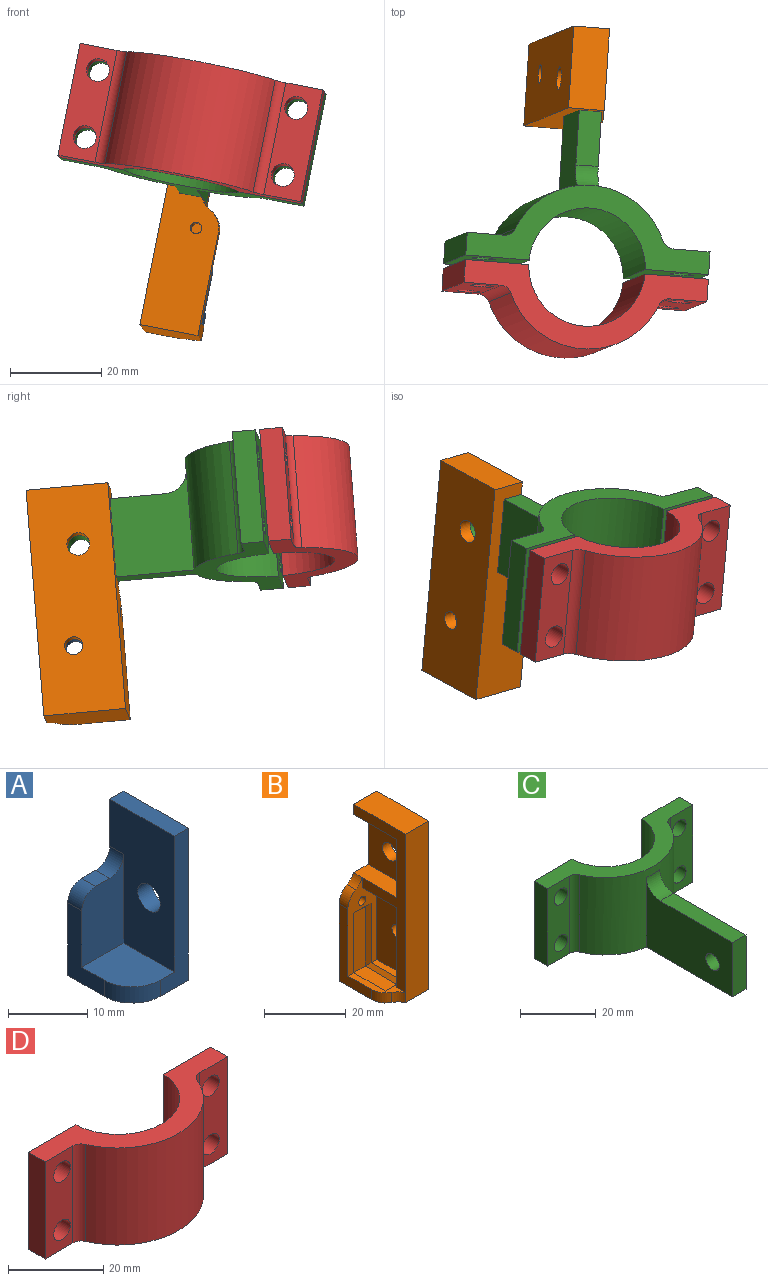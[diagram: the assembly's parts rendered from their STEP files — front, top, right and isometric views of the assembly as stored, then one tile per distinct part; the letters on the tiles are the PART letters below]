
ASSEMBLY  parts=4 mates=3
PART A: 14 faces, bbox 10x11.5x23.5 mm
  f0: plane 23.5x5mm, normal (0,-1,0), area 65mm2, adj f1,f4,f5,f7,f9,f11
  f1: plane 11.5x2.5mm, normal (0,0,1), area 28.8mm2, adj f0,f2,f4,f5
  f2: plane 23.5x10mm, normal (0,1,0), area 161.9mm2, adj f1,f4,f5,f8,f9,f10,f12,f13
  f3: cylinder r=2mm len=4mm, axis (1,0,0), area 31.4mm2, adj f4,f5
  f4: plane 21x11.5mm, normal (-1,0,0), area 194.6mm2, adj f0,f1,f2,f3,f6,f7,f13
  f5: plane 23.5x11.5mm, normal (1,0,0), area 257.7mm2, adj f0,f1,f2,f3,f9
  f6: plane 13.75x7.5mm, normal (0,-1,0), area 84.4mm2, adj f4,f7,f8,f10,f12,f13
  f7: plane 9x7.5mm, normal (0,0,1), area 62.1mm2, adj f0,f4,f6,f10,f11
  f8: plane 2.5x2.5mm, normal (0,0,1), area 6.2mm2, adj f2,f6,f12,f13
  f9: plane 11.5x10mm, normal (0,0,-1), area 109.6mm2, adj f0,f2,f5,f10,f11
  f10: plane 11.25x6.5mm, normal (-1,0,0), area 38.1mm2, adj f2,f6,f7,f9,f11,f12
  f11: cylinder r=5mm len=5mm, axis (0,0,-1), area 19.6mm2, adj f0,f7,f9,f10
  f12: cylinder r=2.5mm len=2.5mm, axis (0,-1,0), area 9.8mm2, adj f2,f6,f8,f10
  f13: cylinder r=2.5mm len=2.5mm, axis (0,1,0), area 9.8mm2, adj f2,f4,f6,f8
PART B: 31 faces, bbox 13x18x50.5 mm
  f0: plane 27x10mm, normal (0,-1,0), area 129.4mm2, adj f3,f11,f15,f16,f17,f19,f20,f22
  f1: plane 24x5mm, normal (0,1,0), area 120mm2, adj f3,f11,f15,f16
  f2: cylinder r=2mm len=4mm, axis (1,0,0), area 37.7mm2, adj f3,f4
  f3: plane 24x12mm, normal (-1,0,0), area 275.4mm2, adj f0,f1,f2,f11,f16
  f4: plane 50.5x18mm, normal (1,0,0), area 876.8mm2, adj f2,f5,f6,f12,f13,f14
  f5: plane 50.5x13mm, normal (0,1,0), area 448.1mm2, adj f4,f7,f8,f10,f12,f14,f15,f17
  f6: cylinder r=2.5mm len=5mm, axis (1,0,0), area 47.1mm2, adj f4,f7
  f7: plane 17.5x15mm, normal (-1,0,0), area 242.9mm2, adj f5,f6,f8,f9,f10
  f8: plane 15x5mm, normal (0,0,1), area 75mm2, adj f5,f7,f9,f15,f19
  f9: plane 17.5x5mm, normal (0,1,0), area 87.5mm2, adj f7,f8,f10,f15
  f10: plane 15x5mm, normal (0,0,-1), area 75mm2, adj f5,f7,f9,f15
  f11: plane 12x5mm, normal (0,0,-1), area 60mm2, adj f0,f1,f3,f15
  f12: plane 18x13mm, normal (0,0,-1), area 220.5mm2, adj f4,f5,f13,f17,f18,f21
  f13: plane 50.5x8mm, normal (0,-1,0), area 404mm2, adj f4,f12,f14,f15,f18
  f14: plane 18x8mm, normal (0,0,1), area 144mm2, adj f4,f5,f13,f15
  f15: plane 47.5x18mm, normal (-1,0,0), area 223.5mm2, adj f0,f1,f5,f8,f9,f10,f11,f13
  f16: plane 15x10mm, normal (0,0,1), area 55.5mm2, adj f0,f1,f3,f15,f17,f18,f21,f28
  f17: plane 23.11x11.11mm, normal (-1,0,0), area 93.7mm2, adj f0,f5,f12,f16,f20,f21
  f18: cylinder r=5mm len=3mm, axis (0,0,1), area 10.2mm2, adj f12,f13,f16,f21
  f19: cylinder r=5mm len=3mm, axis (0,-1,0), area 10.2mm2, adj f0,f5,f8,f20
  f20: cylinder r=5mm len=4.44mm, axis (0,-1,0), area 16.4mm2, adj f0,f5,f17,f19
  f21: cylinder r=5mm len=4.44mm, axis (0,0,1), area 16.4mm2, adj f12,f16,f17,f18
  f22: cylinder r=1.25mm len=3mm, axis (0,-1,0), area 23.6mm2, adj f0,f5
  f23: plane 17.86x4mm, normal (0,-1,0), area 71.4mm2, adj f24,f25,f26,f27
  f24: plane 18.86x1mm, normal (-0.71,-0.71,0), area 25.3mm2, adj f0,f23,f25,f28
  f25: plane 6x1mm, normal (0,-0.71,-0.71), area 7.1mm2, adj f0,f23,f24,f26
  f26: plane 18.86x1mm, normal (0.71,-0.71,0), area 25.3mm2, adj f0,f23,f25,f30
  f27: plane 11x4mm, normal (0,0,1), area 44mm2, adj f23,f28,f29,f30
  f28: plane 12x1mm, normal (-0.71,0,0.71), area 15.6mm2, adj f16,f24,f27,f29
  f29: plane 6x1mm, normal (0,0.71,0.71), area 7.1mm2, adj f16,f27,f28,f30
  f30: plane 12x1mm, normal (0.71,0,0.71), area 15.6mm2, adj f16,f26,f27,f29
PART C: 22 faces, bbox 54.3x49.5x26.1 mm
  f0: cylinder r=18mm len=33.15mm, axis (0,0,-1), area 940mm2, adj f8,f9,f14,f16,f19,f20,f21
  f1: plane 25x8.26mm, normal (0,-1,0), area 167.3mm2, adj f7,f8,f9,f10,f11,f21
  f2: plane 25x8.26mm, normal (0,-1,0), area 167.3mm2, adj f3,f8,f9,f12,f13,f20
  f3: plane 25x5mm, normal (1,0,0), area 125mm2, adj f2,f4,f8,f9
  f4: plane 25x14.15mm, normal (0,1,0), area 314.4mm2, adj f3,f5,f8,f9,f12,f13
  f5: cylinder r=13mm len=25.98mm, axis (0,0,-1), area 996mm2, adj f4,f6,f8,f9
  f6: plane 25x14.15mm, normal (0,1,0), area 314.4mm2, adj f5,f7,f8,f9,f10,f11
  f7: plane 25x5mm, normal (-1,0,0), area 125mm2, adj f1,f6,f8,f9
  f8: plane 54.28x17.5mm, normal (0,0,1), area 334mm2, adj f0,f1,f2,f3,f4,f5,f6,f7
  f9: plane 54.28x49.5mm, normal (0,0,-1), area 494.3mm2, adj f0,f1,f2,f3,f4,f5,f6,f7
  f10: cylinder r=2.5mm len=5mm, axis (0,-1,0), area 78.5mm2, adj f1,f6
  f11: cylinder r=2.5mm len=5mm, axis (0,-1,0), area 78.5mm2, adj f1,f6
  f12: cylinder r=2.5mm len=5mm, axis (0,-1,0), area 78.5mm2, adj f2,f4
  f13: cylinder r=2.5mm len=5mm, axis (0,-1,0), area 78.5mm2, adj f2,f4
  f14: plane 32.17x22.5mm, normal (-1,0,0), area 548.8mm2, adj f0,f9,f15,f17,f18,f19
  f15: plane 17.5x5mm, normal (0,-1,0), area 87.5mm2, adj f9,f14,f16,f17
  f16: plane 32.17x22.5mm, normal (1,0,0), area 548.8mm2, adj f0,f9,f15,f17,f18,f19
  f17: plane 27.14x5mm, normal (0,0,1), area 135.2mm2, adj f14,f15,f16,f19
  f18: cylinder r=2.5mm len=5mm, axis (-1,0,0), area 78.5mm2, adj f14,f16
  f19: torus R=23mm, axis (0,0,1), area 39.4mm2, adj f0,f14,f16,f17
  f20: cylinder r=2.5mm len=25mm, axis (0,0,-1), area 73.1mm2, adj f0,f2,f8,f9
  f21: cylinder r=2.5mm len=25mm, axis (0,0,-1), area 73.1mm2, adj f0,f1,f8,f9
PART D: 16 faces, bbox 54.3x17.5x25 mm
  f0: plane 25x8.26mm, normal (0,-1,0), area 167.3mm2, adj f7,f8,f9,f10,f11,f14
  f1: cylinder r=18mm len=33.15mm, axis (0,0,-1), area 1052.9mm2, adj f8,f9,f14,f15
  f2: plane 25x8.26mm, normal (0,-1,0), area 167.3mm2, adj f3,f8,f9,f12,f13,f15
  f3: plane 25x5mm, normal (1,0,0), area 125mm2, adj f2,f4,f8,f9
  f4: plane 25x14.15mm, normal (0,1,0), area 314.4mm2, adj f3,f5,f8,f9,f12,f13
  f5: cylinder r=13mm len=25.98mm, axis (0,0,-1), area 996mm2, adj f4,f6,f8,f9
  f6: plane 25x14.15mm, normal (0,1,0), area 314.4mm2, adj f5,f7,f8,f9,f10,f11
  f7: plane 25x5mm, normal (-1,0,0), area 125mm2, adj f0,f6,f8,f9
  f8: plane 54.28x17.5mm, normal (0,0,1), area 334mm2, adj f0,f1,f2,f3,f4,f5,f6,f7
  f9: plane 54.28x17.5mm, normal (0,0,-1), area 334mm2, adj f0,f1,f2,f3,f4,f5,f6,f7
  f10: cylinder r=2.5mm len=5mm, axis (0,-1,0), area 78.5mm2, adj f0,f6
  f11: cylinder r=2.5mm len=5mm, axis (0,-1,0), area 78.5mm2, adj f0,f6
  f12: cylinder r=2.5mm len=5mm, axis (0,-1,0), area 78.5mm2, adj f2,f4
  f13: cylinder r=2.5mm len=5mm, axis (0,-1,0), area 78.5mm2, adj f2,f4
  f14: cylinder r=2.5mm len=25mm, axis (0,0,-1), area 73.1mm2, adj f0,f1,f8,f9
  f15: cylinder r=2.5mm len=25mm, axis (0,0,-1), area 73.1mm2, adj f1,f2,f8,f9
PLACE A rot(axis=(0.1,0.04,0.99),175.9deg) t=(-40.48,-59.11,11.33)mm
PLACE B rot(axis=(0.1,0.04,0.99),175.9deg) t=(-40.48,-59.11,11.33)mm
PLACE C rot(axis=(0.1,0.04,0.99),175.9deg) t=(-32.65,-59.74,9.83)mm
PLACE D rot(axis=(-0.38,0.87,-0.32),12.7deg) t=(-31.39,-39.86,8.02)mm
MATE fastened C.f13 <-> D.f11  axis (-0.06,-0.99,0.09) through (-49.16,-36.08,31.69)mm
MATE fastened C.f18 <-> B.f6  axis (-0.98,0.08,0.19) through (-29.71,3.15,11.98)mm
MATE fastened B.f2 <-> A.f3  axis (0.98,-0.08,-0.19) through (-33.9,4.16,-10.28)mm
